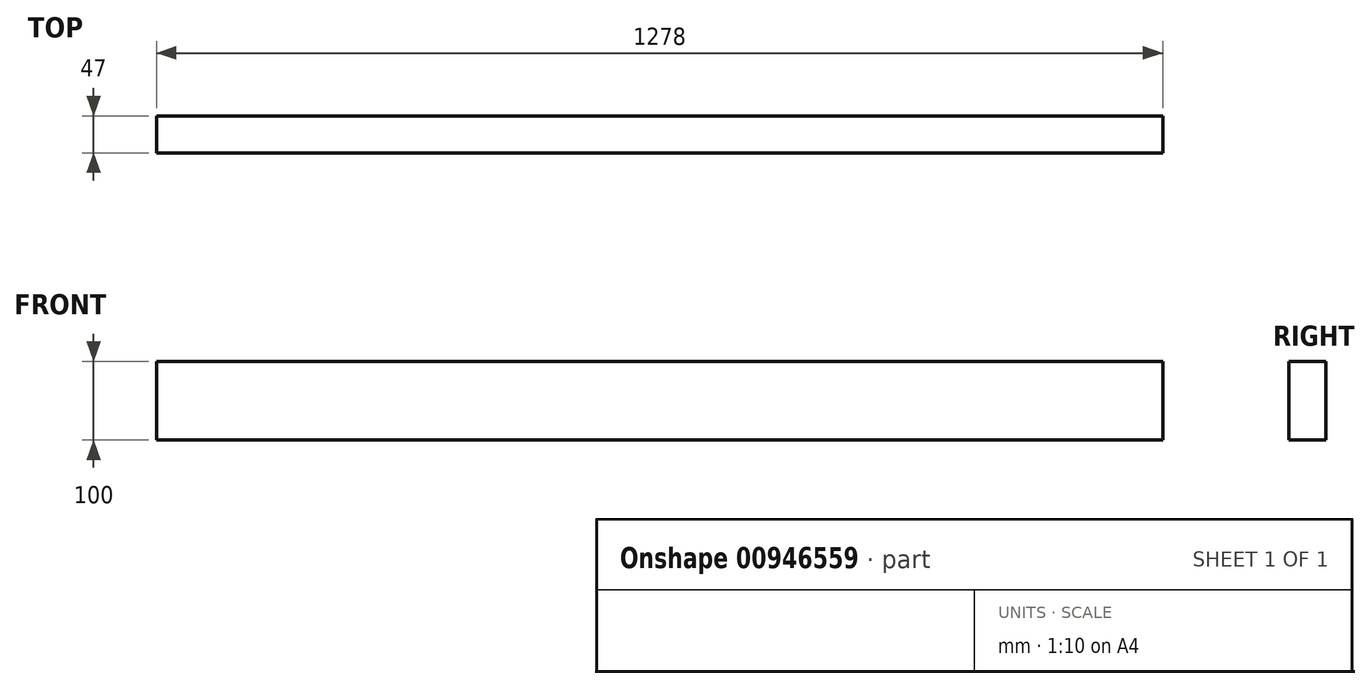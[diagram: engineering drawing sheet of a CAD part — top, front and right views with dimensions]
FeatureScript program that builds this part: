
annotation { "Feature Type Name" : "Feature", "Feature Type Description" : "" }
export const myFeature = defineFeature(function(context is Context, id is Id, definition is map)
    precondition{}
    {
        {
            var Q0;
            Q0=qCreatedBy(makeId("Right.planeOp"),FACE);
            var sketch = newSketch(context, id + "F0", { "sketchPlane" : qUnion([Q0])});
            skLineSegment(sketch, "E0.bottom", {"start": v(0, 0) * mm, "end": v(-47, 0) * mm});
            skLineSegment(sketch, "E0.top", {"start": v(0, 100) * mm, "end": v(-47, 100) * mm});
            skLineSegment(sketch, "E0.left", {"start": v(0, 0) * mm, "end": v(0, 100) * mm});
            skLineSegment(sketch, "E0.right", {"start": v(-47, 0) * mm, "end": v(-47, 100) * mm});
            skSolve(sketch);
        }
        {
            var Q0;
            Q0=qSketchRegion(id+"F0",true);
            extrude(context, id + "F1", {"entities" : qUnion([Q0]), "depth" : 1278 * mm, "offsetDistance" : 25 * mm});
        }
    });
